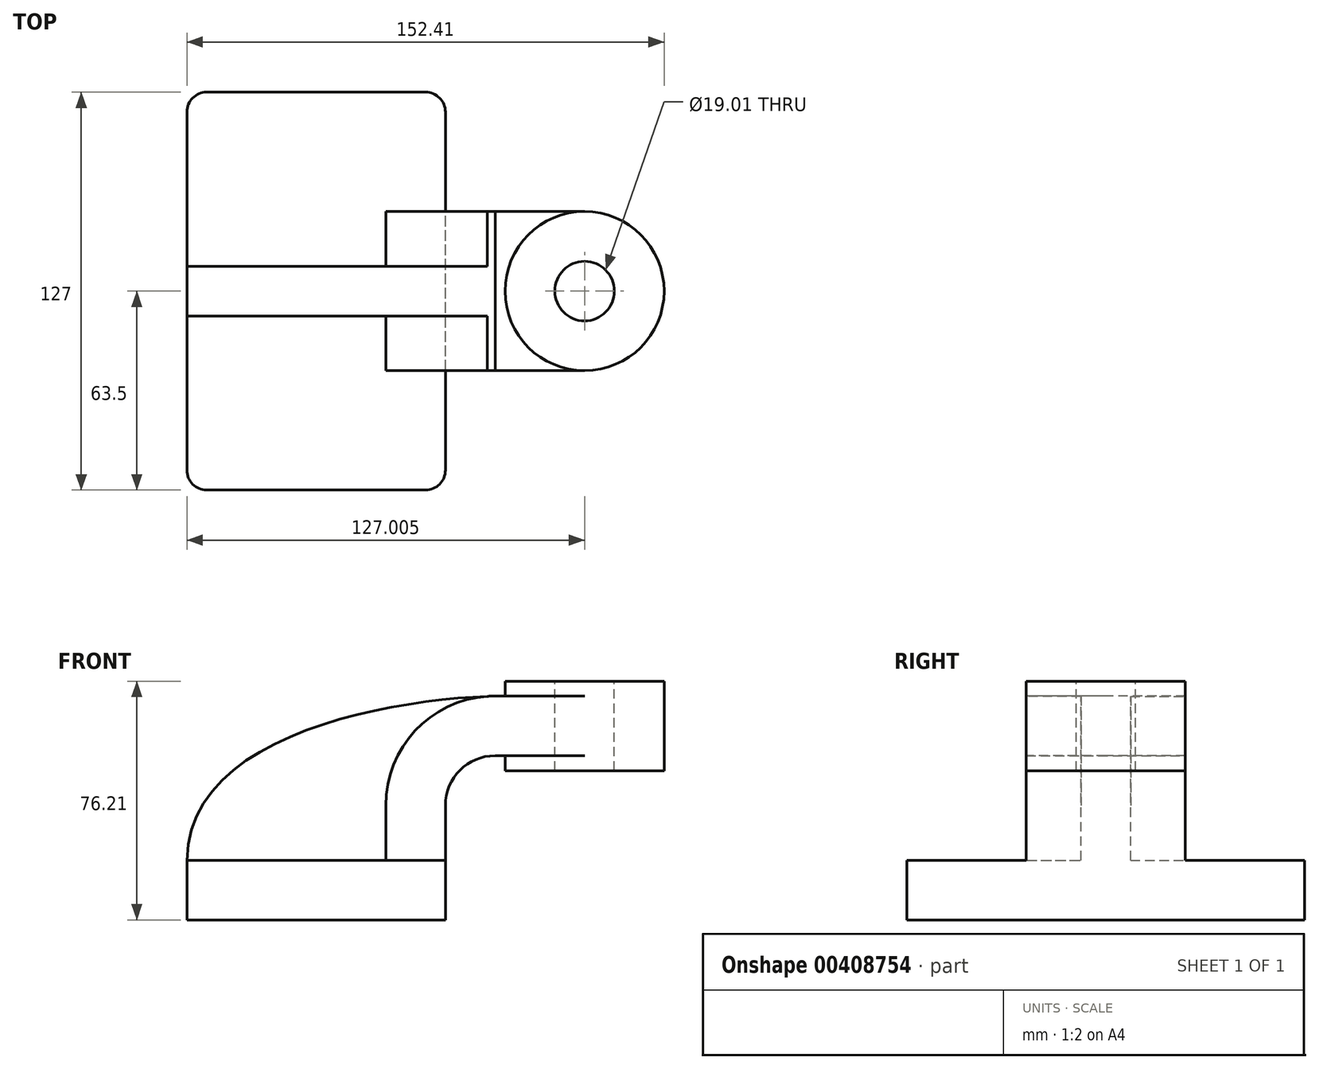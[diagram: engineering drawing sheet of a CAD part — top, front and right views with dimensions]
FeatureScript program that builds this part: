
annotation { "Feature Type Name" : "Feature", "Feature Type Description" : "" }
export const myFeature = defineFeature(function(context is Context, id is Id, definition is map)
    precondition{}
    {
        {
            var Q0;
            Q0=qCreatedBy(makeId("Front.planeOp"),FACE);
            var sketch = newSketch(context, id + "F0", { "sketchPlane" : qUnion([Q0])});
            skLineSegment(sketch, "E0.bottom", {"start": v(-41.28, -9.53) * mm, "end": v(41.28, -9.53) * mm});
            skLineSegment(sketch, "E0.top", {"start": v(-41.28, 9.53) * mm, "end": v(41.28, 9.53) * mm});
            skLineSegment(sketch, "E0.left", {"start": v(-41.28, -9.53) * mm, "end": v(-41.28, 9.53) * mm});
            skLineSegment(sketch, "E0.right", {"start": v(41.28, -9.53) * mm, "end": v(41.28, 9.53) * mm});
            skPoint(sketch, "E0.middle", {"position": v(0, 0) * mm});
            skLineSegment(sketch, "E1.bottom", {"start": v(111.12, 38.1) * mm, "end": v(60.32, 38.1) * mm});
            skLineSegment(sketch, "E1.top", {"start": v(111.12, 66.68) * mm, "end": v(60.32, 66.68) * mm});
            skLineSegment(sketch, "E1.left", {"start": v(111.12, 38.1) * mm, "end": v(111.12, 66.68) * mm});
            skLineSegment(sketch, "E1.right", {"start": v(60.32, 38.1) * mm, "end": v(60.32, 66.68) * mm});
            skPoint(sketch, "E1.middle", {"position": v(85.72, 52.39) * mm});
            skLineSegment(sketch, "E2", {"start": v(41.27, 9.53) * mm, "end": v(41.27, 27) * mm});
            skArc(sketch, "E3", {"start": v(41.27, 27) * mm, "mid": v(45.92, 38.23) * mm, "end": v(57.15, 42.88) * mm});
            skLineSegment(sketch, "E4", {"start": v(57.15, 42.88) * mm, "end": v(85.72, 42.88) * mm});
            skLineSegment(sketch, "E5.0", {"start": v(57.15, 61.93) * mm, "end": v(85.72, 61.93) * mm});
            skArc(sketch, "E5.1", {"start": v(22.23, 27) * mm, "mid": v(32.45, 51.7) * mm, "end": v(57.15, 61.93) * mm});
            skLineSegment(sketch, "E5.2", {"start": v(22.22, 9.53) * mm, "end": v(22.22, 27) * mm});
            skLineSegment(sketch, "E6", {"start": v(85.72, 38.1) * mm, "end": v(85.72, 66.68) * mm});
            skFitSpline(sketch, "E7", {"points": [v(-41.28, 9.53) * mm, v(57.15, 61.93) * mm], "startDerivative": vector(1.01, 121.28) * mm, "endDerivative": vector(99.55, 2.82) * mm});
            skSolve(sketch);
        }
        {
            var Q0;
            Q0=makeQuery(id+"F0.imprint","IMPRINT",FACE,{"disambiguationData":[TD([[makeQuery(id+"F0.imprint","IMPRINT",EDGE,{"derivedFrom":sQuery(id+"F0.wireOp",EDGE,"E0.bottom")}),1.0]])]});
            extrude(context, id + "F1", {"entities" : qUnion([Q0]), "endBound" : BoundingType.SYMMETRIC, "depth" : 127 * mm});
        }
        {
            var Q0;
            {var subQ1=sQuery(id+"F0.wireOp",EDGE,"E2");Q0=makeQuery(id+"F0.imprint","IMPRINT",FACE,{"disambiguationData":[TD([[makeQuery(id+"F0.imprint","IMPRINT",EDGE,{"derivedFrom":subQ1}),1.0]])]});}
            var Q1;
            {var subQ0=sQuery(id+"F0.wireOp",EDGE,"E4");var subQ1=sQuery(id+"F0.wireOp",EDGE,"E1.right");var subQ2=makeQuery(id+"F0.imprint","INTERSECT",VERTEX,{"derivedFrom":[subQ1,subQ0]});Q1=makeQuery(id+"F0.imprint","IMPRINT",FACE,{"disambiguationData":[TD([[makeQuery(id+"F0.imprint","IMPRINT",EDGE,{"disambiguationData":[TD([[subQ2,-1.0]])],"derivedFrom":subQ1}),-1.0]])]});}
            extrude(context, id + "F2", {"entities" : qUnion([Q0, Q1]), "operationType" : NewBodyOperationType.ADD, "endBound" : BoundingType.SYMMETRIC, "depth" : 50.8 * mm});
        }
        {
            var Q0;
            {var subQ3=sQuery(id+"F0.wireOp",EDGE,"E5.2");Q0=makeQuery(id+"F0.imprint","IMPRINT",FACE,{"disambiguationData":[TD([[makeQuery(id+"F0.imprint","IMPRINT",EDGE,{"derivedFrom":subQ3}),1.0]])]});}
            extrude(context, id + "F3", {"entities" : qUnion([Q0]), "operationType" : NewBodyOperationType.ADD, "endBound" : BoundingType.SYMMETRIC, "depth" : 15.88 * mm});
        }
        {
            var Q0;
            {var subQ0=sQuery(id+"F0.wireOp",EDGE,"E1.left");Q0=makeQuery(id+"F0.imprint","IMPRINT",FACE,{"disambiguationData":[TD([[makeQuery(id+"F0.imprint","IMPRINT",EDGE,{"derivedFrom":subQ0}),1.0]])]});}
            var Q1;
            Q1=sQuery(id+"F0.wireOp",EDGE,"E6");
            revolve(context, id + "F4", {"operationType" : NewBodyOperationType.ADD, "entities" : qUnion([Q0]), "axis" : qUnion([Q1]), "revolveType" : RevolveType.FULL});
        }
        {
            var Q0;
            Q0=makeQuery(id+"F1.opExtrude","CAP_EDGE",EDGE,{"disambiguationData":[OSD([sQuery(id+"F0.wireOp",EDGE,"E0.left")])],"isStart":false});
            var Q1;
            Q1=makeQuery(id+"F1.opExtrude","CAP_EDGE",EDGE,{"disambiguationData":[OSD([sQuery(id+"F0.wireOp",EDGE,"E0.right")])],"isStart":false});
            var Q2;
            Q2=makeQuery(id+"F1.opExtrude","CAP_EDGE",EDGE,{"disambiguationData":[OSD([sQuery(id+"F0.wireOp",EDGE,"E0.right")])],"isStart":true});
            var Q3;
            Q3=makeQuery(id+"F1.opExtrude","CAP_EDGE",EDGE,{"disambiguationData":[OSD([sQuery(id+"F0.wireOp",EDGE,"E0.left")])],"isStart":true});
            fillet(context, id + "F5", {"entities" : qUnion([Q0, Q1, Q2, Q3]), "radius" : 6.35 * mm, "tangentPropagation" : true, "allowEdgeOverflow" : false});
        }
        {
            var Q0;
            Q0=makeQuery(id+"F4.opRevolve","SWEPT_FACE",FACE,{"disambiguationData":[OSD([sQuery(id+"F0.wireOp",EDGE,"E1.top")])]});
            var sketch = newSketch(context, id + "F6", { "sketchPlane" : qUnion([Q0])});
            skCircle(sketch, "E8", {"center": v(85.72, 0) * mm, "radius": 9.5 * mm});
            skSolve(sketch);
        }
        {
            var Q0;
            Q0 = qSketchRegion(id + "F6", true);
            extrude(context, id + "F7", {"entities" : qUnion([Q0]), "operationType" : NewBodyOperationType.REMOVE, "endBound" : BoundingType.THROUGH_ALL, "oppositeDirection" : true, "depth" : 25.4 * mm});
        }
    });
